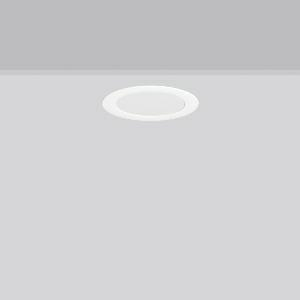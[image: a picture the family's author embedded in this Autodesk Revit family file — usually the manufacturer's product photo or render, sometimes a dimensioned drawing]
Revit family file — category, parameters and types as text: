
# Revit family: toledo_flat_round_e_672223_002_1_54e7
name_source: partatom
category: Lighting Fixtures
units: mm (PartAtom-declared; Revit-internal decimal feet)

## family parameters
Cut with Voids When Loaded = No
Host = Face
Light Source = No
Part Type = Normal
Room Calculation Point = No
Round Connector Dimension = Use Diameter
Shared = No

## types (1)
- TOLEDO FLAT round E (1 x LED Modul 840, 840 lm, 4000)
    Apparent Load = 8 VA
    CIE Flux Codes = 47 79 96 100 100
    Color Rendering = 80
    Color Temperature = 4000
    Default Elevation = 1800 mm
    Description = Series: TOLEDO FLAT round
Ultra thin recessed downlight. For escape route illumination. Housing: die-cast aluminium, powder-coated. Lightguide and diffuser made of non-yellowing plastic (PMMA). Diffuser opal matt plastic. Ceiling installation with spring system. Including separate LED converter with connecting cable 250 mm. Self-contained system with automatic self-test. External driver with simple plug-in locking system. 
Colour: white
Diameter: 190 mm
Height: 2.5 mm
Cut-out diameter: 170 mm
Recess height: 120 mm
Luminaire: recess height: 60-80 mm
Weight: 1.4 kg
Operating mode: maintained power mode
Duration time: 8 h
Lamp: LED
Socket: without socket
Colour temperature: 4000K
Colour rendering index (CRI): 80
System power: 7.7 W
Rated luminous flux: 840 lm
Luminous flux, emergency: 160 lm
System power, emergency: -
Control gear: Regulated power supply
Protection class: I
Type of protection: IP 54
    Height = 0 mm  [stored 0 ft]
    Lamp = 1 x LED Modul 840
    Lamp Light Flux = 840 lm
    Lamp count = 1
    Length = 190 mm  [stored 0.62336 ft]
    Lifetime = 50000 h
    Luminous efficacy = 109 lm/W
    Manufacturer = RZB
    ModVariant = No
    Model = 672223.002.1
    Mounting Place = Ceiling
    Mounting Type = Recessed
    Number of Poles = 1
    OnlyDefault = Yes
    Power Factor = 1
    Product Name = TOLEDO FLAT round E
    Product group = Recessed downlights
    ProductGroupID = 402
    Protection Class = Protection class I
    Protection Degree = IP 40
    RLX_Detail_Level = 1
    RLX_Emergency_Light_Flux = 160 lm
    RLX_Emergency_Type = 3
    RLX_Emergency_Type_DB = Yes
    RlxData = <blob elided: 29057 chars, md5=31747437>
    Socket = socket
    Standby Power = 0 W
    System Light Flux = 840 lm
    System Power = 8 W
    Type Comments = Product without accessories
    Type Image = 901452.002.jpg
    URL = http://relux.com
    VarID = ---
    Voltage = 230 V
    Voltage Range = 220-240 V
    Weight = 0.00 kg
    Width = 0 mm  [stored 0 ft]

note: [stored X ft] marks values corroborated as IEEE doubles in the binary element streams (Revit-internal decimal feet)

## geometry (parser evidence)
native form markers: Blend x4, Sweep x13
no freeform markers — native parametric forms only
